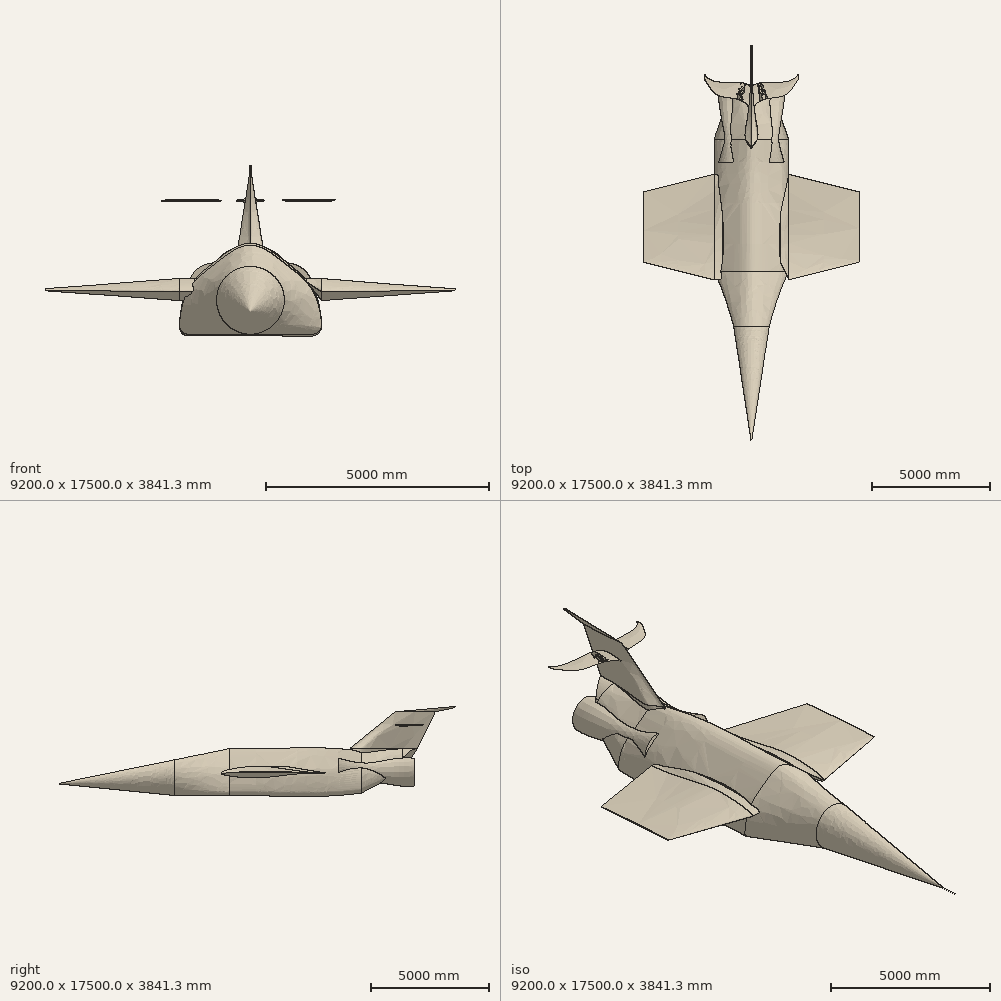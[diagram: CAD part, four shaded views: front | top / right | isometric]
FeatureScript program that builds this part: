
annotation { "Feature Type Name" : "Feature", "Feature Type Description" : "" }
export const myFeature = defineFeature(function(context is Context, id is Id, definition is map)
    precondition{}
    {
        {
            var Q0;
            Q0=qCreatedBy(makeId("Right.planeOp"),FACE);
            var sketch = newSketch(context, id + "F0", { "sketchPlane" : qUnion([Q0])});
            skLineSegment(sketch, "E0", {"start": v(0, 0) * mm, "end": v(-1750, 0) * mm});
            skLineSegment(sketch, "E1", {"start": v(-1750, 0) * mm, "end": v(-3500, 0) * mm});
            skLineSegment(sketch, "E2", {"start": v(-3500, 0) * mm, "end": v(-3500, -1000) * mm});
            skLineSegment(sketch, "E3", {"start": v(-3500, -1000) * mm, "end": v(-8500, -1000) * mm});
            skLineSegment(sketch, "E4", {"start": v(-8500, -1000) * mm, "end": v(-8500, -499.31) * mm});
            skLineSegment(sketch, "E5", {"start": v(-1151.4, 0) * mm, "end": v(-1151.4, 1000) * mm});
            skLineSegment(sketch, "E6", {"start": v(-1151.4, 1000) * mm, "end": v(-8500, -499.31) * mm});
            skLineSegment(sketch, "E7", {"start": v(-8500, -499.31) * mm, "end": v(-3500, -1000) * mm});
            skLineSegment(sketch, "E8", {"start": v(-3500, 0) * mm, "end": v(-3500, 520.82) * mm});
            skLineSegment(sketch, "E9", {"start": v(-8500, -499.31) * mm, "end": v(-8450, -499.31) * mm});
            skLineSegment(sketch, "E10", {"start": v(-8450, -499.31) * mm, "end": v(-8450, -489.1) * mm});
            skLineSegment(sketch, "E11", {"start": v(-8450, -499.31) * mm, "end": v(-8450, -504.32) * mm});
            skSolve(sketch);
        }
        {
            var Q0;
            Q0=sQuery(id+"F0.wireOp",EDGE,"E5");
            cPlane(context, id + "F1", {"entities" : qUnion([Q0]), "cplaneType" : CPlaneType.LINE_ANGLE, "offset" : 25 * mm, "angle" : 90 * degree, "oppositeDirection" : true, "width" : 150 * mm, "height" : 150 * mm});
        }
        {
            var Q0;
            Q0=qCreatedBy(id+"F1.planeOp",FACE);
            var sketch = newSketch(context, id + "F2", { "sketchPlane" : qUnion([Q0])});
            skLineSegment(sketch, "E12.top", {"start": v(-1394.2, -1000) * mm, "end": v(1394.2, -1000) * mm});
            skPoint(sketch, "E12.middle", {"position": v(0, 0) * mm});
            skFitSpline(sketch, "E13", {"points": [v(-1600, -1000) * mm, v(-848, 530) * mm, v(0, 1000) * mm, v(848, 530) * mm, v(1600, -1000) * mm], "startDerivative": vector(0, 10524.75) * mm, "endDerivative": vector(0, -10524.75) * mm});
            skArc(sketch, "E14", {"start": v(-735.27, 618.52) * mm, "mid": v(-1273.27, 435.52) * mm, "end": v(-1440.68, -107.53) * mm});
            skArc(sketch, "E15", {"start": v(1440.68, -107.53) * mm, "mid": v(1273.27, 435.52) * mm, "end": v(735.27, 618.52) * mm});
            skFitSpline(sketch, "E16.trimOffspring", {"points": [v(-1600, -1000) * mm, v(-848, 530) * mm, v(0, 1000) * mm, v(848, 530) * mm, v(1600, -1000) * mm], "startDerivative": vector(0, 10524.75) * mm, "endDerivative": vector(0, -10524.75) * mm});
            skFitSpline(sketch, "E17.trimOffspring", {"points": [v(-1600, -1000) * mm, v(-848, 530) * mm, v(0, 1000) * mm, v(848, 530) * mm, v(1600, -1000) * mm], "startDerivative": vector(0, 10524.75) * mm, "endDerivative": vector(0, -10524.75) * mm});
            skArc(sketch, "E18.filletArc", {"start": v(-1593.82, -787.83) * mm, "mid": v(-1539.85, -937.05) * mm, "end": v(-1394.2, -1000) * mm});
            skArc(sketch, "E19.filletArc", {"start": v(1394.2, -1000) * mm, "mid": v(1539.85, -937.05) * mm, "end": v(1593.82, -787.83) * mm});
            skSolve(sketch);
        }
        {
            var Q0;
            Q0=qCreatedBy(makeId("Front.planeOp"),FACE);
            var sketch = newSketch(context, id + "F3", { "sketchPlane" : qUnion([Q0])});
            skLineSegment(sketch, "E20.top", {"start": v(-1394.2, -1000) * mm, "end": v(1394.2, -1000) * mm});
            skPoint(sketch, "E20.middle", {"position": v(0, 0) * mm});
            skFitSpline(sketch, "E21", {"points": [v(-1600, -1000) * mm, v(-848, 530) * mm, v(0, 1000) * mm, v(848, 530) * mm, v(1600, -1000) * mm], "startDerivative": vector(0, 10524.75) * mm, "endDerivative": vector(0, -10524.75) * mm});
            skArc(sketch, "E22", {"start": v(-735.27, 618.52) * mm, "mid": v(-1273.27, 435.52) * mm, "end": v(-1440.68, -107.53) * mm});
            skArc(sketch, "E23", {"start": v(1440.68, -107.53) * mm, "mid": v(1273.27, 435.52) * mm, "end": v(735.27, 618.52) * mm});
            skFitSpline(sketch, "E24.trimOffspring", {"points": [v(-1600, -1000) * mm, v(-848, 530) * mm, v(0, 1000) * mm, v(848, 530) * mm, v(1600, -1000) * mm], "startDerivative": vector(0, 10524.75) * mm, "endDerivative": vector(0, -10524.75) * mm});
            skFitSpline(sketch, "E25.trimOffspring", {"points": [v(-1600, -1000) * mm, v(-848, 530) * mm, v(0, 1000) * mm, v(848, 530) * mm, v(1600, -1000) * mm], "startDerivative": vector(0, 10524.75) * mm, "endDerivative": vector(0, -10524.75) * mm});
            skArc(sketch, "E26.filletArc", {"start": v(-1593.82, -787.83) * mm, "mid": v(-1539.85, -937.05) * mm, "end": v(-1394.2, -1000) * mm});
            skArc(sketch, "E27.filletArc", {"start": v(1394.2, -1000) * mm, "mid": v(1539.85, -937.05) * mm, "end": v(1593.82, -787.83) * mm});
            skSolve(sketch);
        }
        {
            var Q0;
            Q0=qCreatedBy(makeId("Front.planeOp"),FACE);
            cPlane(context, id + "F4", {"entities" : qUnion([Q0]), "cplaneType" : CPlaneType.OFFSET, "offset" : 3500 * mm, "oppositeDirection" : true, "width" : 150 * mm, "height" : 150 * mm});
        }
        {
            var Q0;
            Q0=qCreatedBy(id+"F4.planeOp",FACE);
            var sketch = newSketch(context, id + "F5", { "sketchPlane" : qUnion([Q0])});
            skLineSegment(sketch, "E28.top", {"start": v(-1394.2, -1000) * mm, "end": v(1394.2, -1000) * mm});
            skPoint(sketch, "E28.middle", {"position": v(0, 0) * mm});
            skFitSpline(sketch, "E29", {"points": [v(-1600, -1000) * mm, v(-848, 530) * mm, v(0, 1000) * mm, v(848, 530) * mm, v(1600, -1000) * mm], "startDerivative": vector(0, 10524.75) * mm, "endDerivative": vector(0, -10524.75) * mm});
            skArc(sketch, "E30", {"start": v(-735.27, 618.52) * mm, "mid": v(-1273.27, 435.52) * mm, "end": v(-1440.68, -107.53) * mm});
            skArc(sketch, "E31", {"start": v(1440.68, -107.53) * mm, "mid": v(1273.27, 435.52) * mm, "end": v(735.27, 618.52) * mm});
            skFitSpline(sketch, "E32.trimOffspring", {"points": [v(-1600, -1000) * mm, v(-848, 530) * mm, v(0, 1000) * mm, v(848, 530) * mm, v(1600, -1000) * mm], "startDerivative": vector(0, 10524.75) * mm, "endDerivative": vector(0, -10524.75) * mm});
            skFitSpline(sketch, "E33.trimOffspring", {"points": [v(-1600, -1000) * mm, v(-848, 530) * mm, v(0, 1000) * mm, v(848, 530) * mm, v(1600, -1000) * mm], "startDerivative": vector(0, 10524.75) * mm, "endDerivative": vector(0, -10524.75) * mm});
            skArc(sketch, "E34.filletArc", {"start": v(-1593.82, -787.83) * mm, "mid": v(-1539.85, -937.05) * mm, "end": v(-1394.2, -1000) * mm});
            skArc(sketch, "E35.filletArc", {"start": v(1394.2, -1000) * mm, "mid": v(1539.85, -937.05) * mm, "end": v(1593.82, -787.83) * mm});
            skSolve(sketch);
        }
        {
            var Q0;
            Q0=qCreatedBy(makeId("Front.planeOp"),FACE);
            cPlane(context, id + "F6", {"entities" : qUnion([Q0]), "cplaneType" : CPlaneType.OFFSET, "offset" : 4500 * mm, "oppositeDirection" : true, "width" : 150 * mm, "height" : 150 * mm});
        }
        {
            var Q0;
            Q0=qCreatedBy(id+"F6.planeOp",FACE);
            var sketch = newSketch(context, id + "F7", { "sketchPlane" : qUnion([Q0])});
            skLineSegment(sketch, "E36.top", {"start": v(-1413.07, -900) * mm, "end": v(1413.07, -900) * mm});
            skPoint(sketch, "E36.middle", {"position": v(0, 0) * mm});
            skFitSpline(sketch, "E37", {"points": [v(-1600, -900) * mm, v(-784.42, 441.24) * mm, v(0, 900) * mm, v(784.42, 441.24) * mm, v(1600, -900) * mm], "startDerivative": vector(0, 9508.62) * mm, "endDerivative": vector(0, -9508.62) * mm});
            skArc(sketch, "E38", {"start": v(-719.25, 488.69) * mm, "mid": v(-1131.76, 394.84) * mm, "end": v(-1324.66, 18.33) * mm});
            skArc(sketch, "E39", {"start": v(1324.66, 18.33) * mm, "mid": v(1131.76, 394.84) * mm, "end": v(719.25, 488.69) * mm});
            skFitSpline(sketch, "E40.trimOffspring", {"points": [v(-1600, -900) * mm, v(-784.42, 441.24) * mm, v(0, 900) * mm, v(784.42, 441.24) * mm, v(1600, -900) * mm], "startDerivative": vector(0, 9508.62) * mm, "endDerivative": vector(0, -9508.62) * mm});
            skFitSpline(sketch, "E41.trimOffspring", {"points": [v(-1600, -900) * mm, v(-784.42, 441.24) * mm, v(0, 900) * mm, v(784.42, 441.24) * mm, v(1600, -900) * mm], "startDerivative": vector(0, 9508.62) * mm, "endDerivative": vector(0, -9508.62) * mm});
            skArc(sketch, "E42.filletArc", {"start": v(-1592.48, -705.43) * mm, "mid": v(-1545.4, -842.02) * mm, "end": v(-1413.07, -900) * mm});
            skArc(sketch, "E43.filletArc", {"start": v(1413.07, -900) * mm, "mid": v(1545.4, -842.02) * mm, "end": v(1592.48, -705.43) * mm});
            skLineSegment(sketch, "E44", {"start": v(-719.25, 488.69) * mm, "end": v(-1324.66, 18.33) * mm, "construction": true});
            skLineSegment(sketch, "E45", {"start": v(719.25, 488.69) * mm, "end": v(1324.66, 18.33) * mm, "construction": true});
            skSolve(sketch);
        }
        {
            var Q0;
            Q0=qCreatedBy(makeId("Front.planeOp"),FACE);
            cPlane(context, id + "F8", {"entities" : qUnion([Q0]), "cplaneType" : CPlaneType.OFFSET, "offset" : 6232.05 * mm, "oppositeDirection" : true, "width" : 150 * mm, "height" : 150 * mm});
        }
        {
            var Q0;
            Q0=qCreatedBy(id+"F8.planeOp",FACE);
            var sketch = newSketch(context, id + "F9", { "sketchPlane" : qUnion([Q0])});
            skArc(sketch, "E46", {"start": v(998.61, 52.63) * mm, "mid": v(0, 1000) * mm, "end": v(-998.61, 52.63) * mm});
            skLineSegment(sketch, "E47", {"start": v(0, 0) * mm, "end": v(-948.68, 0) * mm});
            skLineSegment(sketch, "E48", {"start": v(0, 0) * mm, "end": v(948.68, 0) * mm});
            skLineSegment(sketch, "E49", {"start": v(0, 1000) * mm, "end": v(0, 675) * mm, "construction": true});
            skLineSegment(sketch, "E50", {"start": v(0, 675) * mm, "end": v(-737.82, 675) * mm, "construction": true});
            skLineSegment(sketch, "E51", {"start": v(0, 675) * mm, "end": v(737.82, 675) * mm, "construction": true});
            skPoint(sketch, "E52.visualSharp", {"position": v(-1000, 0) * mm});
            skArc(sketch, "E52.filletArc", {"start": v(-998.61, 52.63) * mm, "mid": v(-984.96, 15.59) * mm, "end": v(-948.68, 0) * mm});
            skPoint(sketch, "E53.visualSharp", {"position": v(1000, 0) * mm});
            skArc(sketch, "E53.filletArc", {"start": v(948.68, 0) * mm, "mid": v(984.96, 15.59) * mm, "end": v(998.61, 52.63) * mm});
            skSolve(sketch);
        }
        {
            var Q0;
            Q0=makeQuery(id+"F2.imprint","IMPRINT",FACE,{"disambiguationData":[TD([[makeQuery(id+"F2.imprint","IMPRINT",EDGE,{"derivedFrom":sQuery(id+"F2.wireOp",EDGE,"E12.top")}),1.0]])]});
            var Q1;
            Q1=makeQuery(id+"F3.imprint","IMPRINT",FACE,{"disambiguationData":[TD([[makeQuery(id+"F3.imprint","IMPRINT",EDGE,{"derivedFrom":sQuery(id+"F3.wireOp",EDGE,"E20.top")}),1.0]])]});
            var Q2;
            Q2=makeQuery(id+"F5.imprint","IMPRINT",FACE,{"disambiguationData":[TD([[makeQuery(id+"F5.imprint","IMPRINT",EDGE,{"derivedFrom":sQuery(id+"F5.wireOp",EDGE,"E28.top")}),1.0]])]});
            var Q3;
            Q3=makeQuery(id+"F7.imprint","IMPRINT",FACE,{"disambiguationData":[TD([[makeQuery(id+"F7.imprint","IMPRINT",EDGE,{"derivedFrom":sQuery(id+"F7.wireOp",EDGE,"E36.top")}),1.0]])]});
            loft(context, id + "F10", {"sheetProfilesArray" : [{ "sheetProfileEntities" : qUnion([Q0]) }, { "sheetProfileEntities" : qUnion([Q1]) }, { "sheetProfileEntities" : qUnion([Q2]) }, { "sheetProfileEntities" : qUnion([Q3]) }]});
        }
        {
            var Q0;
            Q0=sQuery(id+"F7.wireOp",EDGE,"E44");
            var Q1;
            Q1=sQuery(id+"F9.wireOp",VERTEX,"E50.end");
            cPlane(context, id + "F11", {"entities" : qUnion([Q0, Q1]), "cplaneType" : CPlaneType.LINE_ANGLE, "offset" : 25 * mm, "angle" : 180 * degree, "width" : 150 * mm, "height" : 150 * mm});
        }
        {
            var Q0;
            Q0=qCreatedBy(id+"F11.planeOp",FACE);
            var sketch = newSketch(context, id + "F12", { "sketchPlane" : qUnion([Q0])});
            skLineSegment(sketch, "E54", {"start": v(-589.34, 4526.34) * mm, "end": v(-612.8, 6268.32) * mm});
            skLineSegment(sketch, "E55", {"start": v(-1354.08, 4472.19) * mm, "end": v(-612.8, 6268.32) * mm});
            skSolve(sketch);
        }
        {
            var Q0;
            Q0=sQuery(id+"F7.wireOp",EDGE,"E45");
            var Q1;
            Q1=sQuery(id+"F9.wireOp",VERTEX,"E51.end");
            cPlane(context, id + "F13", {"entities" : qUnion([Q0, Q1]), "cplaneType" : CPlaneType.LINE_ANGLE, "offset" : 25 * mm, "angle" : 0 * degree, "width" : 150 * mm, "height" : 150 * mm});
        }
        {
            var Q0;
            Q0=qCreatedBy(id+"F13.planeOp",FACE);
            var sketch = newSketch(context, id + "F14", { "sketchPlane" : qUnion([Q0])});
            skLineSegment(sketch, "E56", {"start": v(589.34, 4526.34) * mm, "end": v(612.8, 6268.32) * mm});
            skLineSegment(sketch, "E57", {"start": v(1354.08, 4472.19) * mm, "end": v(612.8, 6268.32) * mm});
            skSolve(sketch);
        }
        {
            var Q1;
            Q1=makeQuery(id+"F10.opLoft","CAP_FACE",FACE,{"disambiguationData":[OSD([makeQuery(id+"F7.imprint","IMPRINT",FACE,{"disambiguationData":[TD([[makeQuery(id+"F7.imprint","IMPRINT",EDGE,{"derivedFrom":sQuery(id+"F7.wireOp",EDGE,"E36.top")}),1.0]])]})])],"isStart":true});
            var Q2;
            Q2=makeQuery(id+"F9.imprint","IMPRINT",FACE,{"disambiguationData":[TD([[makeQuery(id+"F9.imprint","IMPRINT",EDGE,{"derivedFrom":sQuery(id+"F9.wireOp",EDGE,"E46")}),1.0]])]});
            var Q3;
            Q3=sQuery(id+"F12.wireOp",EDGE,"E54");
            var Q4;
            Q4=sQuery(id+"F14.wireOp",EDGE,"E56");
            loft(context, id + "F15", {"operationType" : NewBodyOperationType.ADD, "addGuides" : true, "sheetProfilesArray" : [{ "sheetProfileEntities" : qUnion([Q1]) }, { "sheetProfileEntities" : qUnion([Q2]) }], "guidesArray" : [{ "guideEntities" : qUnion([Q3]), "guideDerivativeType" : LoftGuideDerivativeType.DEFAULT, "guideDerivativeMagnitude" : 1 }, { "guideEntities" : qUnion([Q4]), "guideDerivativeType" : LoftGuideDerivativeType.DEFAULT, "guideDerivativeMagnitude" : 1 }]});
        }
        {
            var Q0;
            Q0=makeQuery(id+"F15.opLoft","CAP_FACE",FACE,{"disambiguationData":[OSD([makeQuery(id+"F9.imprint","IMPRINT",FACE,{"disambiguationData":[TD([[makeQuery(id+"F9.imprint","IMPRINT",EDGE,{"derivedFrom":sQuery(id+"F9.wireOp",EDGE,"E46")}),1.0]])]})])],"isStart":true});
            extrude(context, id + "F16", {"entities" : qUnion([Q0]), "operationType" : NewBodyOperationType.ADD, "depth" : 649.4 * mm, "offsetDistance" : 25 * mm});
        }
        {
            var Q0;
            Q0=qCreatedBy(makeId("Right.planeOp"),FACE);
            var sketch = newSketch(context, id + "F17", { "sketchPlane" : qUnion([Q0])});
            skLineSegment(sketch, "E58", {"start": v(0, 0) * mm, "end": v(4500, 0) * mm});
            skLineSegment(sketch, "E59", {"start": v(4500, 0) * mm, "end": v(6232.05, 0) * mm});
            skLineSegment(sketch, "E60", {"start": v(4500, 0) * mm, "end": v(4500, 1000) * mm});
            skLineSegment(sketch, "E61", {"start": v(4500, 1000) * mm, "end": v(6881.46, 1000) * mm});
            skLineSegment(sketch, "E62", {"start": v(6881.46, 1000) * mm, "end": v(6881.46, -1000) * mm});
            skLineSegment(sketch, "E63", {"start": v(6881.46, 1000) * mm, "end": v(6232.05, 0) * mm});
            skLineSegment(sketch, "E64", {"start": v(6232.05, 0) * mm, "end": v(5582.64, -1000) * mm});
            skLineSegment(sketch, "E65", {"start": v(5582.64, -1000) * mm, "end": v(6881.46, -1000) * mm});
            skSolve(sketch);
        }
        {
            var Q0;
            Q0=makeQuery(id+"F17.imprint","IMPRINT",FACE,{"disambiguationData":[TD([[makeQuery(id+"F17.imprint","IMPRINT",EDGE,{"derivedFrom":sQuery(id+"F17.wireOp",EDGE,"E62")}),-1.0]])]});
            var Q1;
            Q1=sQuery(id+"F17.wireOp",EDGE,"E61");
            revolve(context, id + "F18", {"operationType" : NewBodyOperationType.REMOVE, "entities" : qUnion([Q0]), "axis" : qUnion([Q1]), "revolveType" : RevolveType.SYMMETRIC, "oppositeDirection" : true, "angle" : 182 * degree});
        }
        {
            var Q0;
            Q0=qCreatedBy(id+"F1.planeOp",FACE);
            var sketch = newSketch(context, id + "F19", { "sketchPlane" : qUnion([Q0])});
            skLineSegment(sketch, "E66.top", {"start": v(-1394.2, -1000) * mm, "end": v(1394.2, -1000) * mm});
            skPoint(sketch, "E66.middle", {"position": v(0, 0) * mm});
            skFitSpline(sketch, "E67", {"points": [v(-1600, -1000) * mm, v(-848, 530) * mm, v(0, 1000) * mm, v(848, 530) * mm, v(1600, -1000) * mm], "startDerivative": vector(0, 10524.75) * mm, "endDerivative": vector(0, -10524.75) * mm});
            skArc(sketch, "E68.filletArc", {"start": v(-1593.82, -787.83) * mm, "mid": v(-1539.85, -937.05) * mm, "end": v(-1394.2, -1000) * mm});
            skArc(sketch, "E69.filletArc", {"start": v(1394.2, -1000) * mm, "mid": v(1539.85, -937.05) * mm, "end": v(1593.82, -787.83) * mm});
            skLineSegment(sketch, "E70", {"start": v(-1593.82, -787.83) * mm, "end": v(-1394.2, -1000) * mm, "construction": true});
            skLineSegment(sketch, "E71", {"start": v(1593.82, -787.83) * mm, "end": v(1394.2, -1000) * mm, "construction": true});
            skSolve(sketch);
        }
        {
            var Q0;
            Q0=qCreatedBy(makeId("Front.planeOp"),FACE);
            cPlane(context, id + "F20", {"entities" : qUnion([Q0]), "cplaneType" : CPlaneType.OFFSET, "offset" : 3500 * mm, "width" : 150 * mm, "height" : 150 * mm});
        }
        {
            var Q0;
            Q0=qCreatedBy(id+"F20.planeOp",FACE);
            var sketch = newSketch(context, id + "F21", { "sketchPlane" : qUnion([Q0])});
            skCircle(sketch, "E72", {"center": v(0, -239.59) * mm, "radius": 760.41 * mm});
            skLineSegment(sketch, "E73", {"start": v(0, -1000) * mm, "end": v(0, -800) * mm, "construction": true});
            skLineSegment(sketch, "E74", {"start": v(0, -800) * mm, "end": v(-513.97, -800) * mm, "construction": true});
            skLineSegment(sketch, "E75", {"start": v(0, -800) * mm, "end": v(513.97, -800) * mm, "construction": true});
            skSolve(sketch);
        }
        {
            var Q0;
            Q0=qCreatedBy(makeId("Front.planeOp"),FACE);
            cPlane(context, id + "F22", {"entities" : qUnion([Q0]), "cplaneType" : CPlaneType.OFFSET, "offset" : 8450 * mm, "width" : 150 * mm, "height" : 150 * mm});
        }
        {
            var Q0;
            Q0=qCreatedBy(id+"F22.planeOp",FACE);
            var sketch = newSketch(context, id + "F23", { "sketchPlane" : qUnion([Q0])});
            skCircle(sketch, "E76", {"center": v(0, -496.71) * mm, "radius": 7.6 * mm});
            skSolve(sketch);
        }
        {
            var Q0;
            Q0=sQuery(id+"F19.wireOp",EDGE,"E70");
            var Q1;
            Q1=sQuery(id+"F21.wireOp",VERTEX,"E74.end");
            cPlane(context, id + "F24", {"entities" : qUnion([Q0, Q1]), "cplaneType" : CPlaneType.LINE_ANGLE, "offset" : 25 * mm, "angle" : 0 * degree, "width" : 150 * mm, "height" : 150 * mm});
        }
        {
            var Q0;
            Q0=qCreatedBy(id+"F24.planeOp",FACE);
            var sketch = newSketch(context, id + "F25", { "sketchPlane" : qUnion([Q0])});
            skLineSegment(sketch, "E77", {"start": v(3032.27, -230.44) * mm, "end": v(558.11, 518.4) * mm});
            skLineSegment(sketch, "E78", {"start": v(3032.27, -230.44) * mm, "end": v(558.11, 227.09) * mm});
            skSolve(sketch);
        }
        {
            var Q0;
            Q0=sQuery(id+"F19.wireOp",EDGE,"E71");
            var Q1;
            Q1=sQuery(id+"F21.wireOp",VERTEX,"E75.end");
            cPlane(context, id + "F26", {"entities" : qUnion([Q0, Q1]), "cplaneType" : CPlaneType.LINE_ANGLE, "offset" : 25 * mm, "angle" : 180 * degree, "width" : 150 * mm, "height" : 150 * mm});
        }
        {
            var Q0;
            Q0=qCreatedBy(id+"F26.planeOp",FACE);
            var sketch = newSketch(context, id + "F27", { "sketchPlane" : qUnion([Q0])});
            skLineSegment(sketch, "E79", {"start": v(-3032.27, -230.44) * mm, "end": v(-558.11, 518.4) * mm});
            skLineSegment(sketch, "E80", {"start": v(-3032.27, -230.44) * mm, "end": v(-558.11, 227.09) * mm});
            skSolve(sketch);
        }
        {
            var Q1;
            Q1=makeQuery(id+"F19.imprint","IMPRINT",FACE,{"disambiguationData":[TD([[makeQuery(id+"F19.imprint","IMPRINT",EDGE,{"derivedFrom":sQuery(id+"F19.wireOp",EDGE,"E66.top")}),1.0]])]});
            var Q2;
            Q2=makeQuery(id+"F21.imprint","IMPRINT",FACE,{"disambiguationData":[TD([[makeQuery(id+"F21.imprint","IMPRINT",EDGE,{"derivedFrom":sQuery(id+"F21.wireOp",EDGE,"E72")}),1.0]])]});
            var Q3;
            Q3=sQuery(id+"F25.wireOp",EDGE,"E77");
            var Q4;
            Q4=sQuery(id+"F27.wireOp",EDGE,"E79");
            loft(context, id + "F28", {"operationType" : NewBodyOperationType.ADD, "addGuides" : true, "sheetProfilesArray" : [{ "sheetProfileEntities" : qUnion([Q1]) }, { "sheetProfileEntities" : qUnion([Q2]) }], "guidesArray" : [{ "guideEntities" : qUnion([Q3]), "guideDerivativeType" : LoftGuideDerivativeType.DEFAULT, "guideDerivativeMagnitude" : 1 }, { "guideEntities" : qUnion([Q4]), "guideDerivativeType" : LoftGuideDerivativeType.DEFAULT, "guideDerivativeMagnitude" : 1 }]});
        }
        {
            var Q1;
            Q1=makeQuery(id+"F28.opLoft","CAP_FACE",FACE,{"disambiguationData":[OSD([makeQuery(id+"F21.imprint","IMPRINT",FACE,{"disambiguationData":[TD([[makeQuery(id+"F21.imprint","IMPRINT",EDGE,{"derivedFrom":sQuery(id+"F21.wireOp",EDGE,"E72")}),1.0]])]})])],"isStart":true});
            var Q2;
            Q2=makeQuery(id+"F23.imprint","IMPRINT",FACE,{"disambiguationData":[TD([[makeQuery(id+"F23.imprint","IMPRINT",EDGE,{"derivedFrom":sQuery(id+"F23.wireOp",EDGE,"E76")}),1.0]])]});
            loft(context, id + "F29", {"operationType" : NewBodyOperationType.ADD, "sheetProfilesArray" : [{ "sheetProfileEntities" : qUnion([Q1]) }, { "sheetProfileEntities" : qUnion([Q2]) }]});
        }
        {
            var Q0;
            Q0=makeQuery(id+"F29.opLoft","CAP_FACE",FACE,{"disambiguationData":[OSD([makeQuery(id+"F23.imprint","IMPRINT",FACE,{"disambiguationData":[TD([[makeQuery(id+"F23.imprint","IMPRINT",EDGE,{"derivedFrom":sQuery(id+"F23.wireOp",EDGE,"E76")}),1.0]])]})])],"isStart":true});
            extrude(context, id + "F30", {"entities" : qUnion([Q0]), "operationType" : NewBodyOperationType.ADD, "depth" : 550 * mm, "offsetDistance" : 25 * mm});
        }
        {
            var Q0;
            Q0=qCreatedBy(makeId("Front.planeOp"),FACE);
            cPlane(context, id + "F31", {"entities" : qUnion([Q0]), "cplaneType" : CPlaneType.OFFSET, "offset" : 3500 * mm, "oppositeDirection" : true, "width" : 150 * mm, "height" : 150 * mm});
        }
        {
            var Q0;
            Q0=qCreatedBy(id+"F31.planeOp",FACE);
            var sketch = newSketch(context, id + "F32", { "sketchPlane" : qUnion([Q0])});
            skCircle(sketch, "E81", {"center": v(-800, 0) * mm, "radius": 600 * mm});
            skCircle(sketch, "E82", {"center": v(800, 0) * mm, "radius": 600 * mm});
            skSolve(sketch);
        }
        {
            var Q0;
            Q0=qCreatedBy(makeId("Front.planeOp"),FACE);
            cPlane(context, id + "F33", {"entities" : qUnion([Q0]), "cplaneType" : CPlaneType.OFFSET, "offset" : 4500 * mm, "oppositeDirection" : true, "width" : 150 * mm, "height" : 150 * mm});
        }
        {
            var Q0;
            Q0=qCreatedBy(id+"F33.planeOp",FACE);
            var sketch = newSketch(context, id + "F34", { "sketchPlane" : qUnion([Q0])});
            skCircle(sketch, "E83", {"center": v(-800, 0) * mm, "radius": 400 * mm});
            skCircle(sketch, "E84", {"center": v(800, 0) * mm, "radius": 400 * mm});
            skSolve(sketch);
        }
        {
            var Q0;
            Q0=qCreatedBy(makeId("Front.planeOp"),FACE);
            cPlane(context, id + "F35", {"entities" : qUnion([Q0]), "cplaneType" : CPlaneType.OFFSET, "offset" : 6232.05 * mm, "oppositeDirection" : true, "width" : 150 * mm, "height" : 150 * mm});
        }
        {
            var Q0;
            Q0=qCreatedBy(id+"F35.planeOp",FACE);
            var sketch = newSketch(context, id + "F36", { "sketchPlane" : qUnion([Q0])});
            skCircle(sketch, "E85", {"center": v(-800, 0) * mm, "radius": 600 * mm});
            skCircle(sketch, "E86", {"center": v(800, 0) * mm, "radius": 600 * mm});
            skSolve(sketch);
        }
        {
            var Q0;
            Q0=qCreatedBy(makeId("Front.planeOp"),FACE);
            cPlane(context, id + "F37", {"entities" : qUnion([Q0]), "cplaneType" : CPlaneType.OFFSET, "offset" : 6732.05 * mm, "oppositeDirection" : true, "width" : 150 * mm, "height" : 150 * mm});
        }
        {
            var Q0;
            Q0=qCreatedBy(id+"F37.planeOp",FACE);
            var sketch = newSketch(context, id + "F38", { "sketchPlane" : qUnion([Q0])});
            skCircle(sketch, "E87", {"center": v(-800, 0) * mm, "radius": 600 * mm});
            skCircle(sketch, "E88", {"center": v(800, 0) * mm, "radius": 600 * mm});
            skSolve(sketch);
        }
        {
            var Q0;
            Q0=makeQuery(id+"F32.imprint","IMPRINT",FACE,{"disambiguationData":[TD([[makeQuery(id+"F32.imprint","IMPRINT",EDGE,{"derivedFrom":sQuery(id+"F32.wireOp",EDGE,"E81")}),1.0]])]});
            var Q1;
            Q1=makeQuery(id+"F34.imprint","IMPRINT",FACE,{"disambiguationData":[TD([[makeQuery(id+"F34.imprint","IMPRINT",EDGE,{"derivedFrom":sQuery(id+"F34.wireOp",EDGE,"E83")}),1.0]])]});
            var Q2;
            Q2=makeQuery(id+"F36.imprint","IMPRINT",FACE,{"disambiguationData":[TD([[makeQuery(id+"F36.imprint","IMPRINT",EDGE,{"derivedFrom":sQuery(id+"F36.wireOp",EDGE,"E85")}),1.0]])]});
            var Q3;
            Q3=makeQuery(id+"F38.imprint","IMPRINT",FACE,{"disambiguationData":[TD([[makeQuery(id+"F38.imprint","IMPRINT",EDGE,{"derivedFrom":sQuery(id+"F38.wireOp",EDGE,"E87")}),1.0]])]});
            loft(context, id + "F39", {"sheetProfilesArray" : [{ "sheetProfileEntities" : qUnion([Q0]) }, { "sheetProfileEntities" : qUnion([Q1]) }, { "sheetProfileEntities" : qUnion([Q2]) }, { "sheetProfileEntities" : qUnion([Q3]) }]});
        }
        {
            var Q0;
            Q0=makeQuery(id+"F32.imprint","IMPRINT",FACE,{"disambiguationData":[TD([[makeQuery(id+"F32.imprint","IMPRINT",EDGE,{"derivedFrom":sQuery(id+"F32.wireOp",EDGE,"E82")}),1.0]])]});
            var Q1;
            Q1=makeQuery(id+"F34.imprint","IMPRINT",FACE,{"disambiguationData":[TD([[makeQuery(id+"F34.imprint","IMPRINT",EDGE,{"derivedFrom":sQuery(id+"F34.wireOp",EDGE,"E84")}),1.0]])]});
            var Q2;
            Q2=makeQuery(id+"F36.imprint","IMPRINT",FACE,{"disambiguationData":[TD([[makeQuery(id+"F36.imprint","IMPRINT",EDGE,{"derivedFrom":sQuery(id+"F36.wireOp",EDGE,"E86")}),1.0]])]});
            var Q3;
            Q3=makeQuery(id+"F38.imprint","IMPRINT",FACE,{"disambiguationData":[TD([[makeQuery(id+"F38.imprint","IMPRINT",EDGE,{"derivedFrom":sQuery(id+"F38.wireOp",EDGE,"E88")}),1.0]])]});
            loft(context, id + "F40", {"sheetProfilesArray" : [{ "sheetProfileEntities" : qUnion([Q0]) }, { "sheetProfileEntities" : qUnion([Q1]) }, { "sheetProfileEntities" : qUnion([Q2]) }, { "sheetProfileEntities" : qUnion([Q3]) }]});
        }
        {
            var Q0;
            Q0=qCreatedBy(makeId("Right.planeOp"),FACE);
            var sketch = newSketch(context, id + "F41", { "sketchPlane" : qUnion([Q0])});
            skFitSpline(sketch, "E89", {"points": [v(-1500, -50) * mm, v(0, 250) * mm, v(3000, -50) * mm, v(0, -250) * mm, v(-1500, -50) * mm]});
            skSolve(sketch);
        }
        {
            var Q0;
            Q0=qCreatedBy(makeId("Right.planeOp"),FACE);
            cPlane(context, id + "F42", {"entities" : qUnion([Q0]), "cplaneType" : CPlaneType.OFFSET, "offset" : 1600 * mm, "oppositeDirection" : true, "width" : 150 * mm, "height" : 150 * mm});
        }
        {
            var Q0;
            Q0=qCreatedBy(id+"F42.planeOp",FACE);
            var sketch = newSketch(context, id + "F43", { "sketchPlane" : qUnion([Q0])});
            skFitSpline(sketch, "E90", {"points": [v(-1500, -50) * mm, v(0, 250) * mm, v(3000, -50) * mm], "startDerivative": vector(0, 887.04) * mm, "endDerivative": vector(7705.35, -256.85) * mm});
            skFitSpline(sketch, "E91", {"points": [v(-1500, -50) * mm, v(0, -250) * mm, v(3000, -50) * mm], "startDerivative": vector(0, -722.87) * mm, "endDerivative": vector(7692.49, -256.42) * mm});
            skSolve(sketch);
        }
        {
            var Q0;
            Q0=qCreatedBy(makeId("Right.planeOp"),FACE);
            cPlane(context, id + "F44", {"entities" : qUnion([Q0]), "cplaneType" : CPlaneType.OFFSET, "offset" : 1600 * mm, "width" : 150 * mm, "height" : 150 * mm});
        }
        {
            var Q0;
            Q0=qCreatedBy(id+"F44.planeOp",FACE);
            var sketch = newSketch(context, id + "F45", { "sketchPlane" : qUnion([Q0])});
            skFitSpline(sketch, "E92", {"points": [v(-1500, -50) * mm, v(0, 250) * mm, v(3000, -50) * mm], "startDerivative": vector(0, 887.04) * mm, "endDerivative": vector(7705.35, -256.85) * mm});
            skFitSpline(sketch, "E93", {"points": [v(-1500, -50) * mm, v(0, -250) * mm, v(3000, -50) * mm], "startDerivative": vector(0, -722.87) * mm, "endDerivative": vector(7692.49, -256.42) * mm});
            skSolve(sketch);
        }
        {
            var Q0;
            Q0=qCreatedBy(makeId("Right.planeOp"),FACE);
            cPlane(context, id + "F46", {"entities" : qUnion([Q0]), "cplaneType" : CPlaneType.OFFSET, "offset" : 4600 * mm, "oppositeDirection" : true, "width" : 150 * mm, "height" : 150 * mm});
        }
        {
            var Q0;
            Q0=qCreatedBy(id+"F46.planeOp",FACE);
            var sketch = newSketch(context, id + "F47", { "sketchPlane" : qUnion([Q0])});
            skFitSpline(sketch, "E94", {"points": [v(-750, -10) * mm, v(250, 25) * mm, v(2250, -10) * mm], "startDerivative": vector(0, 162.94) * mm, "endDerivative": vector(5121.8, -51.22) * mm});
            skFitSpline(sketch, "E95", {"points": [v(-750, -10) * mm, v(750, -25) * mm, v(2250, -10) * mm], "startDerivative": vector(0, -60) * mm, "endDerivative": vector(6000, 0) * mm});
            skSolve(sketch);
        }
        {
            var Q0;
            Q0=qCreatedBy(makeId("Right.planeOp"),FACE);
            cPlane(context, id + "F48", {"entities" : qUnion([Q0]), "cplaneType" : CPlaneType.OFFSET, "offset" : 4600 * mm, "width" : 150 * mm, "height" : 150 * mm});
        }
        {
            var Q0;
            Q0=qCreatedBy(id+"F48.planeOp",FACE);
            var sketch = newSketch(context, id + "F49", { "sketchPlane" : qUnion([Q0])});
            skFitSpline(sketch, "E96", {"points": [v(-750, -10) * mm, v(250, 25) * mm, v(2250, -10) * mm], "startDerivative": vector(0, 253.46) * mm, "endDerivative": vector(3841.36, -51.22) * mm});
            skFitSpline(sketch, "E97", {"points": [v(-750, -10) * mm, v(750, -25) * mm, v(2250, -10) * mm], "startDerivative": vector(0, -45) * mm, "endDerivative": vector(4500, 0) * mm});
            skSolve(sketch);
        }
        {
            var Q0;
            Q0=qSketchRegion(id+"F41",true);
            extrude(context, id + "F50", {"entities" : qUnion([Q0]), "endBound" : BoundingType.SYMMETRIC, "depth" : 2500 * mm, "offsetDistance" : 25 * mm});
        }
        {
            var Q1;
            Q1=makeQuery(id+"F50.opExtrude","CAP_FACE",FACE,{"disambiguationData":[OSD([sQuery(id+"F41.wireOp",EDGE,"E89")])],"isStart":true});
            var Q2;
            {var subQ0=sQuery(id+"F43.wireOp",EDGE,"E90");Q2=makeQuery(id+"F43.imprint","IMPRINT",FACE,{"disambiguationData":[TD([[makeQuery(id+"F43.imprint","IMPRINT",EDGE,{"derivedFrom":subQ0}),-1.0]])]});}
            loft(context, id + "F51", {"operationType" : NewBodyOperationType.ADD, "sheetProfilesArray" : [{ "sheetProfileEntities" : qUnion([Q1]) }, { "sheetProfileEntities" : qUnion([Q2]) }]});
        }
        {
            var Q1;
            Q1=makeQuery(id+"F50.opExtrude","CAP_FACE",FACE,{"disambiguationData":[OSD([sQuery(id+"F41.wireOp",EDGE,"E89")])],"isStart":false});
            var Q2;
            {var subQ0=sQuery(id+"F45.wireOp",EDGE,"E92");Q2=makeQuery(id+"F45.imprint","IMPRINT",FACE,{"disambiguationData":[TD([[makeQuery(id+"F45.imprint","IMPRINT",EDGE,{"derivedFrom":subQ0}),-1.0]])]});}
            loft(context, id + "F52", {"operationType" : NewBodyOperationType.ADD, "sheetProfilesArray" : [{ "sheetProfileEntities" : qUnion([Q1]) }, { "sheetProfileEntities" : qUnion([Q2]) }]});
        }
        {
            var Q1;
            {var subQ0=sQuery(id+"F43.wireOp",EDGE,"E90");Q1=makeQuery(id+"F51.opLoft","CAP_FACE",FACE,{"disambiguationData":[OSD([makeQuery(id+"F43.imprint","IMPRINT",FACE,{"disambiguationData":[TD([[makeQuery(id+"F43.imprint","IMPRINT",EDGE,{"derivedFrom":subQ0}),-1.0]])]})])],"isStart":true});}
            var Q2;
            Q2=makeQuery(id+"F47.imprint","IMPRINT",FACE,{"disambiguationData":[TD([[makeQuery(id+"F47.imprint","IMPRINT",EDGE,{"derivedFrom":sQuery(id+"F47.wireOp",EDGE,"E94")}),-1.0]])]});
            loft(context, id + "F53", {"operationType" : NewBodyOperationType.ADD, "sheetProfilesArray" : [{ "sheetProfileEntities" : qUnion([Q1]) }, { "sheetProfileEntities" : qUnion([Q2]) }]});
        }
        {
            var Q1;
            {var subQ0=sQuery(id+"F45.wireOp",EDGE,"E92");Q1=makeQuery(id+"F52.opLoft","CAP_FACE",FACE,{"disambiguationData":[OSD([makeQuery(id+"F45.imprint","IMPRINT",FACE,{"disambiguationData":[TD([[makeQuery(id+"F45.imprint","IMPRINT",EDGE,{"derivedFrom":subQ0}),-1.0]])]})])],"isStart":true});}
            var Q2;
            Q2=makeQuery(id+"F49.imprint","IMPRINT",FACE,{"disambiguationData":[TD([[makeQuery(id+"F49.imprint","IMPRINT",EDGE,{"derivedFrom":sQuery(id+"F49.wireOp",EDGE,"E96")}),-1.0]])]});
            loft(context, id + "F54", {"operationType" : NewBodyOperationType.ADD, "sheetProfilesArray" : [{ "sheetProfileEntities" : qUnion([Q1]) }, { "sheetProfileEntities" : qUnion([Q2]) }]});
        }
        {
            var Q0;
            Q0=qCreatedBy(makeId("Right.planeOp"),FACE);
            var sketch = newSketch(context, id + "F55", { "sketchPlane" : qUnion([Q0])});
            skLineSegment(sketch, "E98", {"start": v(0, 0) * mm, "end": v(4500, 0) * mm});
            skLineSegment(sketch, "E99", {"start": v(4500, 0) * mm, "end": v(4500, 1000) * mm});
            skLineSegment(sketch, "E100", {"start": v(4500, 1000) * mm, "end": v(4500, 750) * mm});
            skLineSegment(sketch, "E101", {"start": v(4500, 750) * mm, "end": v(4000, 750) * mm});
            skLineSegment(sketch, "E102", {"start": v(4500, 750) * mm, "end": v(6250, 750) * mm});
            skLineSegment(sketch, "E103", {"start": v(4500, 1000) * mm, "end": v(4000, 1000) * mm});
            skLineSegment(sketch, "E104", {"start": v(4500, 1000) * mm, "end": v(6881.46, 1000) * mm});
            skLineSegment(sketch, "E105", {"start": v(6881.46, 1000) * mm, "end": v(8500, 1000) * mm});
            skLineSegment(sketch, "E106", {"start": v(8500, 1000) * mm, "end": v(8500, 2800) * mm});
            skLineSegment(sketch, "E107", {"start": v(6881.46, 1000) * mm, "end": v(7648.6, 2572.89) * mm});
            skLineSegment(sketch, "E108", {"start": v(7648.6, 2572.89) * mm, "end": v(5943.2, 2572.89) * mm});
            skLineSegment(sketch, "E109", {"start": v(4000, 1000) * mm, "end": v(5943.2, 2572.89) * mm});
            skSolve(sketch);
        }
        {
            var Q0;
            Q0=qCreatedBy(makeId("Top.planeOp"),FACE);
            cPlane(context, id + "F56", {"entities" : qUnion([Q0]), "cplaneType" : CPlaneType.OFFSET, "offset" : 750 * mm, "width" : 150 * mm, "height" : 150 * mm});
        }
        {
            var Q0;
            Q0=qCreatedBy(id+"F56.planeOp",FACE);
            var sketch = newSketch(context, id + "F57", { "sketchPlane" : qUnion([Q0])});
            skFitSpline(sketch, "E110", {"points": [v(0, 4000) * mm, v(-250, 4500) * mm, v(0, 6250) * mm], "startDerivative": vector(-889.86, 1147.1) * mm, "endDerivative": vector(737.87, 3164.53) * mm});
            skFitSpline(sketch, "E111", {"points": [v(0, 4000) * mm, v(250, 4500) * mm, v(0, 6250) * mm], "startDerivative": vector(889.86, 1147.1) * mm, "endDerivative": vector(-737.87, 3164.53) * mm});
            skSolve(sketch);
        }
        {
            var Q0;
            Q0=qCreatedBy(makeId("Top.planeOp"),FACE);
            cPlane(context, id + "F58", {"entities" : qUnion([Q0]), "cplaneType" : CPlaneType.OFFSET, "offset" : 1000 * mm, "width" : 150 * mm, "height" : 150 * mm});
        }
        {
            var Q0;
            Q0=qCreatedBy(id+"F58.planeOp",FACE);
            var sketch = newSketch(context, id + "F59", { "sketchPlane" : qUnion([Q0])});
            skFitSpline(sketch, "E112", {"points": [v(0, 4000) * mm, v(-250, 4500) * mm, v(0, 6881.46) * mm], "startDerivative": vector(0, 2302.24) * mm, "endDerivative": vector(0, 5298.17) * mm});
            skFitSpline(sketch, "E113", {"points": [v(0, 4000) * mm, v(250, 4500) * mm, v(0, 6881.46) * mm], "startDerivative": vector(0, 2302.24) * mm, "endDerivative": vector(0, 5298.17) * mm});
            skSolve(sketch);
        }
        {
            var Q0;
            Q0=sQuery(id+"F55.wireOp",EDGE,"E108");
            cPlane(context, id + "F60", {"entities" : qUnion([Q0]), "cplaneType" : CPlaneType.LINE_ANGLE, "offset" : 25 * mm, "angle" : 180 * degree, "width" : 150 * mm, "height" : 150 * mm});
        }
        {
            var Q0;
            Q0=qCreatedBy(id+"F60.planeOp",FACE);
            var sketch = newSketch(context, id + "F61", { "sketchPlane" : qUnion([Q0])});
            skFitSpline(sketch, "E114", {"points": [v(0, 5943.2) * mm, v(-25, 6795.9) * mm, v(0, 7648.6) * mm], "startDerivative": vector(-75, 1705.4) * mm, "endDerivative": vector(75, 1705.4) * mm});
            skFitSpline(sketch, "E115", {"points": [v(0, 5943.2) * mm, v(25, 6795.9) * mm, v(0, 7648.6) * mm], "startDerivative": vector(75, 1705.4) * mm, "endDerivative": vector(-75, 1705.4) * mm});
            skSolve(sketch);
        }
        {
            var Q0;
            Q0=qCreatedBy(makeId("Front.planeOp"),FACE);
            cPlane(context, id + "F62", {"entities" : qUnion([Q0]), "cplaneType" : CPlaneType.OFFSET, "offset" : 8500 * mm, "oppositeDirection" : true, "width" : 150 * mm, "height" : 150 * mm});
        }
        {
            var Q0;
            Q0=qCreatedBy(id+"F62.planeOp",FACE);
            var sketch = newSketch(context, id + "F63", { "sketchPlane" : qUnion([Q0])});
            skCircle(sketch, "E116", {"center": v(0, 2775) * mm, "radius": 25 * mm});
            skSolve(sketch);
        }
        {
            var Q0;
            Q0=qCreatedBy(makeId("Right.planeOp"),FACE);
            var sketch = newSketch(context, id + "F64", { "sketchPlane" : qUnion([Q0])});
            skLineSegment(sketch, "E117", {"start": v(5943.2, 2572.89) * mm, "end": v(8500, 2800) * mm});
            skSolve(sketch);
        }
        {
            var Q1;
            Q1 = qSketchRegion(id + "F57", true);
            var Q2;
            Q2 = qSketchRegion(id + "F59", true);
            loft(context, id + "F65", {"sheetProfilesArray" : [{ "sheetProfileEntities" : qUnion([Q1]) }, { "sheetProfileEntities" : qUnion([Q2]) }]});
        }
        {
            var Q1;
            {var subQ0=sQuery(id+"F59.wireOp",EDGE,"E112");Q1=makeQuery(id+"F65.opLoft","CAP_FACE",FACE,{"disambiguationData":[OSD([makeQuery(id+"F59.imprint","IMPRINT",FACE,{"disambiguationData":[TD([[makeQuery(id+"F59.imprint","IMPRINT",EDGE,{"derivedFrom":subQ0}),-1.0]])]})])],"isStart":true});}
            var Q2;
            Q2=makeQuery(id+"F61.imprint","IMPRINT",FACE,{"disambiguationData":[TD([[makeQuery(id+"F61.imprint","IMPRINT",EDGE,{"derivedFrom":sQuery(id+"F61.wireOp",EDGE,"E114")}),-1.0]])]});
            loft(context, id + "F66", {"operationType" : NewBodyOperationType.ADD, "sheetProfilesArray" : [{ "sheetProfileEntities" : qUnion([Q1]) }, { "sheetProfileEntities" : qUnion([Q2]) }]});
        }
        {
            var Q1;
            Q1=makeQuery(id+"F66.opLoft","CAP_FACE",FACE,{"disambiguationData":[OSD([makeQuery(id+"F61.imprint","IMPRINT",FACE,{"disambiguationData":[TD([[makeQuery(id+"F61.imprint","IMPRINT",EDGE,{"derivedFrom":sQuery(id+"F61.wireOp",EDGE,"E114")}),-1.0]])]})])],"isStart":true});
            var Q2;
            Q2=makeQuery(id+"F63.imprint","IMPRINT",FACE,{"disambiguationData":[TD([[makeQuery(id+"F63.imprint","IMPRINT",EDGE,{"derivedFrom":sQuery(id+"F63.wireOp",EDGE,"E116")}),1.0]])]});
            var Q3;
            Q3=sQuery(id+"F64.wireOp",EDGE,"E117");
            loft(context, id + "F67", {"operationType" : NewBodyOperationType.ADD, "addGuides" : true, "sheetProfilesArray" : [{ "sheetProfileEntities" : qUnion([Q1]) }, { "sheetProfileEntities" : qUnion([Q2]) }], "guidesArray" : [{ "guideEntities" : qUnion([Q3]), "guideDerivativeType" : LoftGuideDerivativeType.DEFAULT, "guideDerivativeMagnitude" : 1 }]});
        }
        {
            var Q0;
            Q0=qCreatedBy(makeId("Top.planeOp"),FACE);
            cPlane(context, id + "F68", {"entities" : qUnion([Q0]), "cplaneType" : CPlaneType.OFFSET, "offset" : 2000 * mm, "width" : 150 * mm, "height" : 150 * mm});
        }
        {
            var Q0;
            Q0=qCreatedBy(id+"F68.planeOp",FACE);
            var sketch = newSketch(context, id + "F69", { "sketchPlane" : qUnion([Q0])});
            skLineSegment(sketch, "E118", {"start": v(0, 0) * mm, "end": v(0, 4500) * mm});
            skLineSegment(sketch, "E119", {"start": v(0, 4500) * mm, "end": v(0, 7369.2) * mm});
            skLineSegment(sketch, "E120", {"start": v(0, 7369.2) * mm, "end": v(0, 5235.43) * mm});
            skLineSegment(sketch, "E121", {"start": v(0, 6302.31) * mm, "end": v(0, 5302.31) * mm});
            skLineSegment(sketch, "E122", {"start": v(0, 6302.31) * mm, "end": v(0, 7302.31) * mm});
            skLineSegment(sketch, "E123", {"start": v(0, 6302.31) * mm, "end": v(0, 6552.31) * mm});
            skLineSegment(sketch, "E124", {"start": v(0, 6302.31) * mm, "end": v(-1200, 6302.31) * mm});
            skLineSegment(sketch, "E125", {"start": v(0, 6302.31) * mm, "end": v(1200, 6302.31) * mm});
            skLineSegment(sketch, "E126", {"start": v(0, 6552.31) * mm, "end": v(-1700, 6552.31) * mm});
            skLineSegment(sketch, "E127", {"start": v(0, 6552.31) * mm, "end": v(1700, 6552.31) * mm});
            skLineSegment(sketch, "E128", {"start": v(0, 7302.31) * mm, "end": v(-2000, 7302.31) * mm});
            skLineSegment(sketch, "E129", {"start": v(0, 7302.31) * mm, "end": v(2000, 7302.31) * mm});
            skLineSegment(sketch, "E130", {"start": v(-2000, 7302.31) * mm, "end": v(-2000, 7052.31) * mm});
            skLineSegment(sketch, "E131", {"start": v(2000, 7302.31) * mm, "end": v(2000, 7052.31) * mm});
            skFitSpline(sketch, "E132", {"points": [v(0, 5302.31) * mm, v(-1200, 6302.31) * mm, v(-2000, 7052.31) * mm], "startDerivative": vector(0, 5513.6) * mm, "endDerivative": vector(-1974.16, 3290.27) * mm});
            skFitSpline(sketch, "E133", {"points": [v(0, 5302.31) * mm, v(1200, 6302.31) * mm, v(2000, 7052.31) * mm], "startDerivative": vector(0, 5513.6) * mm, "endDerivative": vector(1974.16, 3290.27) * mm});
            skFitSpline(sketch, "E134", {"points": [v(0, 6552.31) * mm, v(-2000, 7302.31) * mm], "startDerivative": vector(0, 2250) * mm, "endDerivative": vector(-900, 2250) * mm});
            skFitSpline(sketch, "E135", {"points": [v(0, 6552.31) * mm, v(2000, 7302.31) * mm], "startDerivative": vector(0, 2250) * mm, "endDerivative": vector(900, 2250) * mm});
            skSolve(sketch);
        }
        {
            var Q0;
            Q0=qCreatedBy(makeId("Right.planeOp"),FACE);
            var sketch = newSketch(context, id + "F70", { "sketchPlane" : qUnion([Q0])});
            skFitSpline(sketch, "E136", {"points": [v(5302.31, 2000) * mm, v(5927.31, 2050) * mm, v(6552.31, 2000) * mm], "startDerivative": vector(1250, 150) * mm, "endDerivative": vector(1250, -150) * mm});
            skFitSpline(sketch, "E137", {"points": [v(5302.31, 2000) * mm, v(5927.31, 1950) * mm, v(6552.31, 2000) * mm], "startDerivative": vector(1250, -150) * mm, "endDerivative": vector(1250, 150) * mm});
            skSolve(sketch);
        }
        {
            var Q0;
            Q0=qCreatedBy(makeId("Right.planeOp"),FACE);
            cPlane(context, id + "F71", {"entities" : qUnion([Q0]), "cplaneType" : CPlaneType.OFFSET, "offset" : 2000 * mm, "oppositeDirection" : true, "width" : 150 * mm, "height" : 150 * mm});
        }
        {
            var Q0;
            Q0=qCreatedBy(id+"F71.planeOp",FACE);
            var sketch = newSketch(context, id + "F72", { "sketchPlane" : qUnion([Q0])});
            skFitSpline(sketch, "E138", {"points": [v(7052.31, 2000) * mm, v(7177.31, 2010) * mm, v(7302.31, 2000) * mm], "startDerivative": vector(250, 30) * mm, "endDerivative": vector(250, -30) * mm});
            skFitSpline(sketch, "E139", {"points": [v(7052.31, 2000) * mm, v(7177.31, 1990) * mm, v(7302.31, 2000) * mm], "startDerivative": vector(250, -30) * mm, "endDerivative": vector(250, 30) * mm});
            skSolve(sketch);
        }
        {
            var Q0;
            Q0=qCreatedBy(makeId("Right.planeOp"),FACE);
            cPlane(context, id + "F73", {"entities" : qUnion([Q0]), "cplaneType" : CPlaneType.OFFSET, "offset" : 2000 * mm, "width" : 150 * mm, "height" : 150 * mm});
        }
        {
            var Q0;
            Q0=qCreatedBy(id+"F73.planeOp",FACE);
            var sketch = newSketch(context, id + "F74", { "sketchPlane" : qUnion([Q0])});
            skFitSpline(sketch, "E140", {"points": [v(7052.31, 2000) * mm, v(7177.31, 2010) * mm, v(7302.31, 2000) * mm], "startDerivative": vector(250, 30) * mm, "endDerivative": vector(250, -30) * mm});
            skFitSpline(sketch, "E141", {"points": [v(7052.31, 2000) * mm, v(7177.31, 1990) * mm, v(7302.31, 2000) * mm], "startDerivative": vector(250, -30) * mm, "endDerivative": vector(250, 30) * mm});
            skSolve(sketch);
        }
        {
            var Q1;
            Q1 = qSketchRegion(id + "F70", true);
            var Q2;
            Q2=makeQuery(id+"F72.imprint","IMPRINT",FACE,{"disambiguationData":[TD([[makeQuery(id+"F72.imprint","IMPRINT",EDGE,{"derivedFrom":sQuery(id+"F72.wireOp",EDGE,"E138")}),-1.0]])]});
            var Q3;
            Q3=sQuery(id+"F69.wireOp",EDGE,"E132");
            var Q4;
            Q4=sQuery(id+"F69.wireOp",EDGE,"E134");
            loft(context, id + "F75", {"addGuides" : true, "sheetProfilesArray" : [{ "sheetProfileEntities" : qUnion([Q1]) }, { "sheetProfileEntities" : qUnion([Q2]) }], "guidesArray" : [{ "guideEntities" : qUnion([Q3]), "guideDerivativeType" : LoftGuideDerivativeType.DEFAULT, "guideDerivativeMagnitude" : 1 }, { "guideEntities" : qUnion([Q4]), "guideDerivativeType" : LoftGuideDerivativeType.DEFAULT, "guideDerivativeMagnitude" : 1 }]});
        }
        {
            var Q1;
            Q1 = qSketchRegion(id + "F70", true);
            var Q2;
            Q2=makeQuery(id+"F74.imprint","IMPRINT",FACE,{"disambiguationData":[TD([[makeQuery(id+"F74.imprint","IMPRINT",EDGE,{"derivedFrom":sQuery(id+"F74.wireOp",EDGE,"E140")}),-1.0]])]});
            var Q3;
            Q3=sQuery(id+"F69.wireOp",EDGE,"E133");
            var Q4;
            Q4=sQuery(id+"F69.wireOp",EDGE,"E135");
            loft(context, id + "F76", {"operationType" : NewBodyOperationType.ADD, "addGuides" : true, "sheetProfilesArray" : [{ "sheetProfileEntities" : qUnion([Q1]) }, { "sheetProfileEntities" : qUnion([Q2]) }], "guidesArray" : [{ "guideEntities" : qUnion([Q3]), "guideDerivativeType" : LoftGuideDerivativeType.DEFAULT, "guideDerivativeMagnitude" : 1 }, { "guideEntities" : qUnion([Q4]), "guideDerivativeType" : LoftGuideDerivativeType.DEFAULT, "guideDerivativeMagnitude" : 1 }]});
        }
    });
